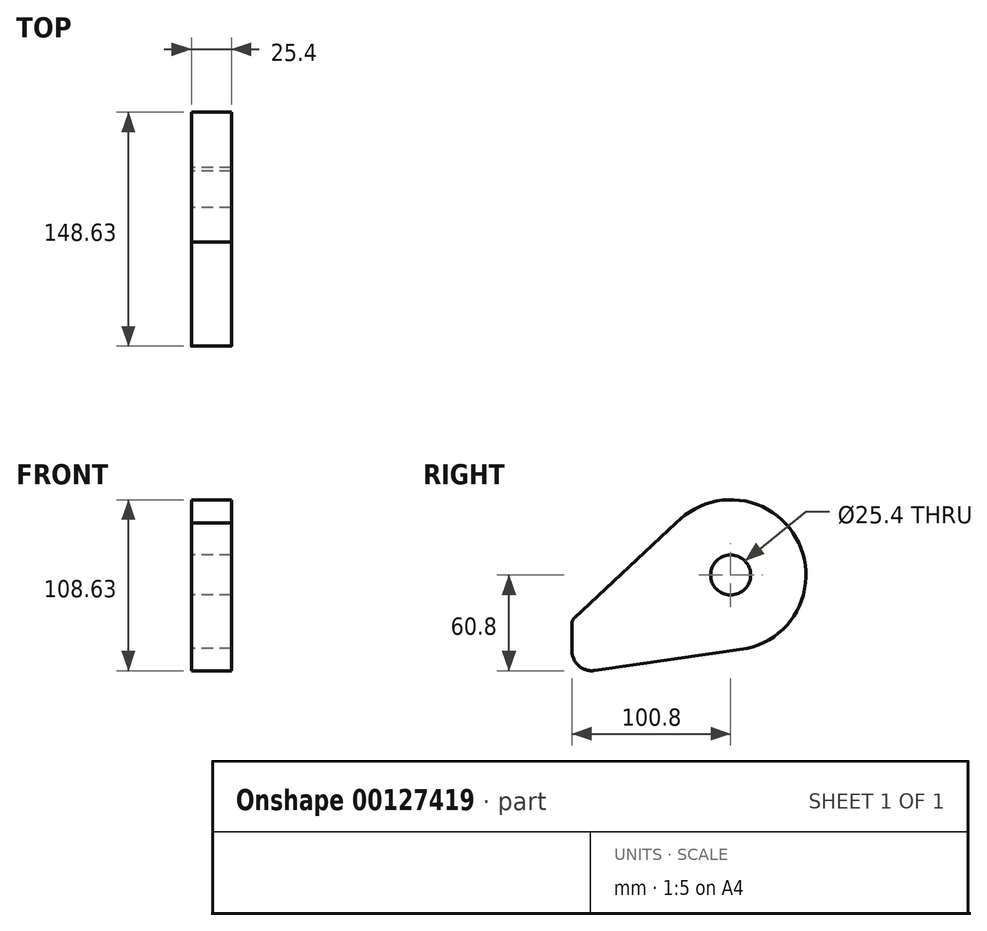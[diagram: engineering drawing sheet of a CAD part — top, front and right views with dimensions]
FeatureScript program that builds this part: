
annotation { "Feature Type Name" : "Feature", "Feature Type Description" : "" }
export const myFeature = defineFeature(function(context is Context, id is Id, definition is map)
    precondition{}
    {
        {
            var Q0;
            Q0=qCreatedBy(makeId("Right.planeOp"),FACE);
            var sketch = newSketch(context, id + "F0", { "sketchPlane" : qUnion([Q0])});
            skArc(sketch, "E0", {"start": v(3.24, -47.72) * mm, "mid": v(43.3, 20.34) * mm, "end": v(-34.66, 32.96) * mm});
            skLineSegment(sketch, "E1", {"start": v(-34.66, 32.96) * mm, "end": v(-100.8, -28.7) * mm});
            skLineSegment(sketch, "E2", {"start": v(-100.8, -62.77) * mm, "end": v(-100.8, -28.7) * mm});
            skLineSegment(sketch, "E3", {"start": v(-100.8, -62.77) * mm, "end": v(10.42, -46.68) * mm});
            skSolve(sketch);
        }
        {
            var Q0;
            {var subQ4=sQuery(id+"F0.wireOp",EDGE,"E1");Q0=makeQuery(id+"F0.imprint","IMPRINT",FACE,{"disambiguationData":[TD([[makeQuery(id+"F0.imprint","IMPRINT",EDGE,{"derivedFrom":subQ4}),1.0]])]});}
            extrude(context, id + "F1", {"entities" : qUnion([Q0]), "depth" : 25.4 * mm});
        }
        {
            var Q0;
            Q0=makeQuery(id+"F1.opExtrude","SWEPT_EDGE",EDGE,{"disambiguationData":[OSD([sQuery(id+"F0.wireOp",EDGE,"E1"),sQuery(id+"F0.wireOp",EDGE,"E2")])]});
            fillet(context, id + "F2", {"entities" : qUnion([Q0]), "radius" : 5.08 * mm, "tangentPropagation" : true, "allowEdgeOverflow" : false});
        }
        {
            var Q0;
            Q0=makeQuery(id+"F1.opExtrude","SWEPT_EDGE",EDGE,{"disambiguationData":[OSD([sQuery(id+"F0.wireOp",EDGE,"E2"),sQuery(id+"F0.wireOp",EDGE,"E3")])]});
            fillet(context, id + "F3", {"entities" : qUnion([Q0]), "radius" : 12.7 * mm, "tangentPropagation" : true, "allowEdgeOverflow" : false});
        }
        {
            var Q0;
            Q0=makeQuery(id+"F1.opExtrude","CAP_FACE",FACE,{"disambiguationData":[OSD([sQuery(id+"F0.wireOp",EDGE,"E0"),sQuery(id+"F0.wireOp",EDGE,"E1"),sQuery(id+"F0.wireOp",EDGE,"E2"),sQuery(id+"F0.wireOp",EDGE,"E3")])],"isStart":true});
            var sketch = newSketch(context, id + "F4", { "sketchPlane" : qUnion([Q0])});
            skCircle(sketch, "E4", {"center": v(0, 0) * mm, "radius": 28.5 * mm});
            skSolve(sketch);
        }
        {
            var Q0;
            Q0=sQuery(id+"F4.wireOp",VERTEX,"E4.center");
            var Q1;
            Q1=makeQuery(id+"F1.opExtrude","SWEPT_BODY",BODY,{"disambiguationData":[OSD([sQuery(id+"F0.wireOp",EDGE,"E0"),sQuery(id+"F0.wireOp",EDGE,"E1"),sQuery(id+"F0.wireOp",EDGE,"E2"),sQuery(id+"F0.wireOp",EDGE,"E3")])]});
            hole(context, id + "F5", {"style" : HoleStyle.SIMPLE, "endStyle" : HoleEndStyle.THROUGH, "holeDiameter" : 25.4 * mm, "locations" : qUnion([Q0]), "scope" : qUnion([Q1]), "isTappedThrough" : true});
        }
    });
